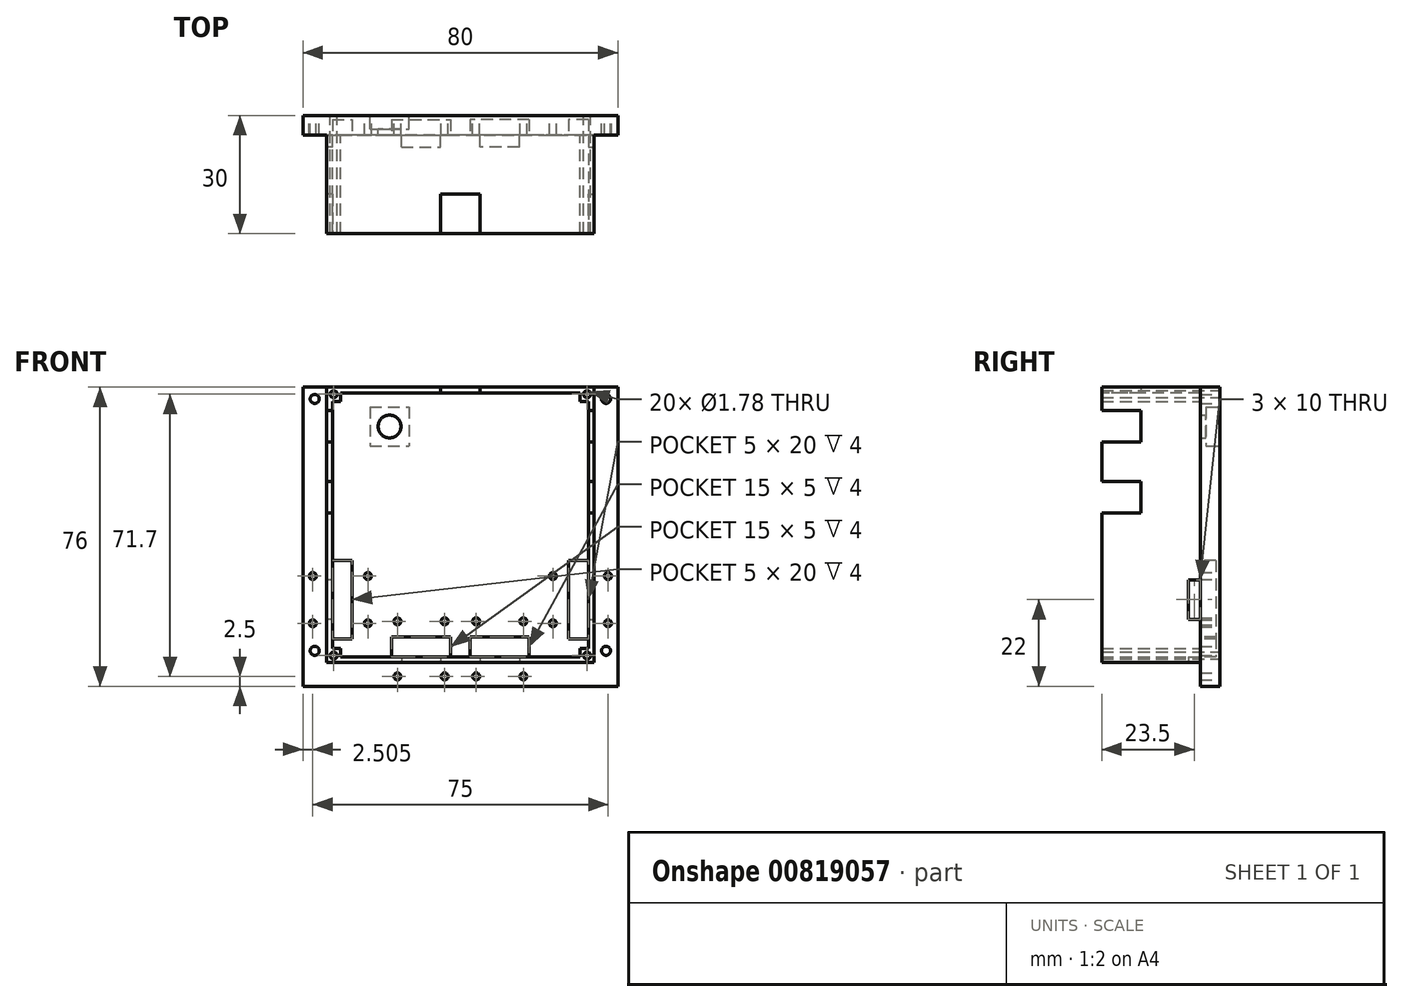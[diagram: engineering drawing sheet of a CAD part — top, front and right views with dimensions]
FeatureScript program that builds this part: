
annotation { "Feature Type Name" : "Feature", "Feature Type Description" : "" }
export const myFeature = defineFeature(function(context is Context, id is Id, definition is map)
    precondition{}
    {
        {
            var Q0;
            Q0=qCreatedBy(makeId("Front.planeOp"),FACE);
            var sketch = newSketch(context, id + "F0", { "sketchPlane" : qUnion([Q0])});
            skCircle(sketch, "E0", {"center": v(-20.58, 35.7) * mm, "radius": 0.89 * mm});
            skCircle(sketch, "E1", {"center": v(-25.88, -10.5) * mm, "radius": 0.89 * mm});
            skCircle(sketch, "E2", {"center": v(-11.88, -10.5) * mm, "radius": 0.89 * mm});
            skCircle(sketch, "E3", {"center": v(-11.88, -22.5) * mm, "radius": 0.89 * mm});
            skCircle(sketch, "E4", {"center": v(-25.88, -22.5) * mm, "radius": 0.89 * mm});
            skCircle(sketch, "E5", {"center": v(-25.38, -29.5) * mm, "radius": 1.14 * mm});
            skLineSegment(sketch, "E6", {"start": v(51.62, 37.5) * mm, "end": v(-28.38, 37.5) * mm});
            skLineSegment(sketch, "E7", {"start": v(-28.37, 37.5) * mm, "end": v(-28.38, -32.5) * mm});
            skLineSegment(sketch, "E8", {"start": v(51.63, -32.5) * mm, "end": v(-28.38, -32.5) * mm});
            skLineSegment(sketch, "E9.bottom", {"start": v(-28.38, -32.5) * mm, "end": v(-22.38, -32.5) * mm, "construction": true});
            skLineSegment(sketch, "E9.top", {"start": v(-28.38, -26.5) * mm, "end": v(-22.38, -26.5) * mm, "construction": true});
            skLineSegment(sketch, "E9.left", {"start": v(-28.38, -32.5) * mm, "end": v(-28.38, -26.5) * mm, "construction": true});
            skLineSegment(sketch, "E9.right", {"start": v(-22.38, -32.5) * mm, "end": v(-22.38, -26.5) * mm, "construction": true});
            skLineSegment(sketch, "E10", {"start": v(-28.37, -26.5) * mm, "end": v(-22.38, -32.5) * mm});
            skLineSegment(sketch, "E11", {"start": v(-28.38, -32.5) * mm, "end": v(-22.38, -26.5) * mm});
            skPoint(sketch, "E12", {"position": v(-28.38, 2.5) * mm});
            skLineSegment(sketch, "E13", {"start": v(11.62, 37.5) * mm, "end": v(-20.58, 37.5) * mm, "construction": true});
            skLineSegment(sketch, "E14", {"start": v(-20.58, 37.5) * mm, "end": v(-20.58, 35.7) * mm});
            skLineSegment(sketch, "E15", {"start": v(-11.88, -10.5) * mm, "end": v(-11.88, -22.5) * mm, "construction": true});
            skPoint(sketch, "E16", {"position": v(-11.88, -16.5) * mm});
            skLineSegment(sketch, "E17", {"start": v(-11.88, -16.5) * mm, "end": v(-28.38, -16.5) * mm, "construction": true});
            skLineSegment(sketch, "E18", {"start": v(-25.88, -22.5) * mm, "end": v(-25.88, -10.5) * mm, "construction": true});
            skPoint(sketch, "E19", {"position": v(-25.88, -16.5) * mm});
            skPoint(sketch, "E20", {"position": v(-20.88, -16.5) * mm});
            skLineSegment(sketch, "E21", {"start": v(-20.88, -16.5) * mm, "end": v(-20.88, -6.5) * mm, "construction": true});
            skLineSegment(sketch, "E22", {"start": v(-20.88, -6.5) * mm, "end": v(-15.88, -6.5) * mm, "construction": true});
            skLineSegment(sketch, "E23", {"start": v(-15.88, -6.5) * mm, "end": v(-15.88, -26.5) * mm, "construction": true});
            skLineSegment(sketch, "E24.bottom", {"start": v(-20.88, -6.5) * mm, "end": v(-15.88, -6.5) * mm});
            skLineSegment(sketch, "E24.top", {"start": v(-20.88, -26.5) * mm, "end": v(-15.88, -26.5) * mm});
            skLineSegment(sketch, "E24.left", {"start": v(-20.88, -6.5) * mm, "end": v(-20.88, -26.5) * mm});
            skLineSegment(sketch, "E24.right", {"start": v(-15.88, -6.5) * mm, "end": v(-15.88, -26.5) * mm});
            skLineSegment(sketch, "E25", {"start": v(-25.88, -10.5) * mm, "end": v(-28.38, -10.5) * mm, "construction": true});
            skLineSegment(sketch, "E26", {"start": v(-20.88, -6.5) * mm, "end": v(-28.38, -6.5) * mm, "construction": true});
            skLineSegment(sketch, "E27", {"start": v(51.62, 37.5) * mm, "end": v(51.63, -32.5) * mm});
            skLineSegment(sketch, "E28", {"start": v(11.62, 37.5) * mm, "end": v(11.62, 27.5) * mm, "construction": true});
            skLineSegment(sketch, "E29.bottom", {"start": v(-28.38, 37.5) * mm, "end": v(-22.38, 37.5) * mm, "construction": true});
            skLineSegment(sketch, "E29.top", {"start": v(-28.38, 31.5) * mm, "end": v(-22.38, 31.5) * mm, "construction": true});
            skLineSegment(sketch, "E29.left", {"start": v(-28.38, 37.5) * mm, "end": v(-28.38, 31.5) * mm, "construction": true});
            skLineSegment(sketch, "E29.right", {"start": v(-22.38, 37.5) * mm, "end": v(-22.38, 31.5) * mm, "construction": true});
            skLineSegment(sketch, "E30", {"start": v(-28.38, 37.5) * mm, "end": v(-22.38, 31.5) * mm, "construction": true});
            skLineSegment(sketch, "E31", {"start": v(-28.38, 31.5) * mm, "end": v(-22.38, 37.5) * mm, "construction": true});
            skCircle(sketch, "E32", {"center": v(-25.38, 34.5) * mm, "radius": 1.14 * mm});
            skCircle(sketch, "E33.MirrorC", {"center": v(48.62, -29.5) * mm, "radius": 1.14 * mm});
            skCircle(sketch, "E34.MirrorC", {"center": v(49.13, -22.5) * mm, "radius": 0.89 * mm});
            skLineSegment(sketch, "E35.MirrorCS", {"start": v(39.13, -6.5) * mm, "end": v(39.13, -26.5) * mm});
            skLineSegment(sketch, "E36.MirrorCS", {"start": v(44.13, -6.5) * mm, "end": v(39.13, -6.5) * mm});
            skLineSegment(sketch, "E37.MirrorCS", {"start": v(44.13, -6.5) * mm, "end": v(44.13, -26.5) * mm});
            skPoint(sketch, "E38.MirrorP", {"position": v(44.13, -16.5) * mm});
            skLineSegment(sketch, "E39.MirrorCS", {"start": v(44.13, -6.5) * mm, "end": v(39.13, -6.5) * mm, "construction": true});
            skLineSegment(sketch, "E40.MirrorCS", {"start": v(35.12, -10.5) * mm, "end": v(35.12, -22.5) * mm, "construction": true});
            skLineSegment(sketch, "E41.MirrorCS", {"start": v(44.13, -26.5) * mm, "end": v(39.13, -26.5) * mm});
            skLineSegment(sketch, "E42.MirrorCS", {"start": v(44.13, -16.5) * mm, "end": v(44.13, -6.5) * mm, "construction": true});
            skCircle(sketch, "E43.MirrorC", {"center": v(35.12, -22.5) * mm, "radius": 0.89 * mm});
            skCircle(sketch, "E44.MirrorC", {"center": v(35.12, -10.5) * mm, "radius": 0.89 * mm});
            skPoint(sketch, "E45.MirrorP", {"position": v(49.13, -16.5) * mm});
            skPoint(sketch, "E46.MirrorP", {"position": v(35.12, -16.5) * mm});
            skCircle(sketch, "E47.MirrorC", {"center": v(49.13, -10.5) * mm, "radius": 0.89 * mm});
            skLineSegment(sketch, "E48.MirrorCS", {"start": v(49.12, -22.5) * mm, "end": v(49.12, -10.5) * mm, "construction": true});
            skLineSegment(sketch, "E49.MirrorCS", {"start": v(39.13, -6.5) * mm, "end": v(39.13, -26.5) * mm, "construction": true});
            skPoint(sketch, "E50.MirrorP", {"position": v(51.63, 2.5) * mm});
            skCircle(sketch, "E51.MirrorC", {"center": v(48.63, 34.5) * mm, "radius": 1.14 * mm});
            skCircle(sketch, "E52.MirrorC", {"center": v(43.83, 35.7) * mm, "radius": 0.89 * mm});
            skLineSegment(sketch, "E53", {"start": v(44.13, -26.5) * mm, "end": v(45.63, -26.5) * mm, "construction": true});
            skLineSegment(sketch, "E54", {"start": v(45.63, -26.5) * mm, "end": v(45.63, -32.5) * mm});
            skLineSegment(sketch, "E55", {"start": v(45.63, -26.5) * mm, "end": v(45.63, 37.5) * mm});
            skLineSegment(sketch, "E56", {"start": v(-20.88, -26.5) * mm, "end": v(-22.38, -26.5) * mm, "construction": true});
            skLineSegment(sketch, "E57.bottom", {"start": v(-22.38, 37.5) * mm, "end": v(45.62, 37.5) * mm});
            skLineSegment(sketch, "E57.top", {"start": v(-22.38, -32.5) * mm, "end": v(45.63, -32.5) * mm});
            skLineSegment(sketch, "E57.left", {"start": v(-22.38, 37.5) * mm, "end": v(-22.38, -32.5) * mm});
            skLineSegment(sketch, "E57.right", {"start": v(45.63, 37.5) * mm, "end": v(45.63, -32.5) * mm});
            skLineSegment(sketch, "E58", {"start": v(-20.58, 35.7) * mm, "end": v(-18.78, 35.7) * mm, "construction": true});
            skLineSegment(sketch, "E59", {"start": v(-18.78, 35.7) * mm, "end": v(-18.78, 33.9) * mm, "construction": true});
            skLineSegment(sketch, "E60.bottom", {"start": v(-18.78, 33.9) * mm, "end": v(-22.38, 33.9) * mm});
            skLineSegment(sketch, "E60.top", {"start": v(-18.78, 37.5) * mm, "end": v(-22.38, 37.5) * mm});
            skLineSegment(sketch, "E60.left", {"start": v(-18.78, 33.9) * mm, "end": v(-18.78, 37.5) * mm});
            skLineSegment(sketch, "E60.right", {"start": v(-22.38, 33.9) * mm, "end": v(-22.38, 37.5) * mm});
            skLineSegment(sketch, "E61", {"start": v(43.83, 35.7) * mm, "end": v(42.02, 35.7) * mm, "construction": true});
            skLineSegment(sketch, "E62", {"start": v(42.03, 35.7) * mm, "end": v(42.03, 33.9) * mm, "construction": true});
            skLineSegment(sketch, "E63.bottom", {"start": v(42.02, 33.9) * mm, "end": v(45.62, 33.9) * mm});
            skLineSegment(sketch, "E63.top", {"start": v(42.02, 37.5) * mm, "end": v(45.62, 37.5) * mm});
            skLineSegment(sketch, "E63.left", {"start": v(42.03, 33.9) * mm, "end": v(42.03, 37.5) * mm});
            skLineSegment(sketch, "E63.right", {"start": v(45.63, 33.9) * mm, "end": v(45.63, 37.5) * mm});
            skLineSegment(sketch, "E64", {"start": v(11.63, -32.5) * mm, "end": v(13.43, -32.5) * mm});
            skLineSegment(sketch, "E65", {"start": v(44.13, -16.5) * mm, "end": v(47.13, -16.5) * mm, "construction": true});
            skLineSegment(sketch, "E66.bottom", {"start": v(43.13, -11.5) * mm, "end": v(47.13, -11.5) * mm});
            skLineSegment(sketch, "E66.top", {"start": v(43.13, -21.5) * mm, "end": v(47.13, -21.5) * mm});
            skLineSegment(sketch, "E66.left", {"start": v(43.13, -11.5) * mm, "end": v(43.13, -21.5) * mm});
            skLineSegment(sketch, "E66.right", {"start": v(47.13, -11.5) * mm, "end": v(47.13, -21.5) * mm});
            skPoint(sketch, "E67", {"position": v(47.13, -16.5) * mm});
            skLineSegment(sketch, "E68.MirrorCS", {"start": v(-19.88, -21.5) * mm, "end": v(-23.88, -21.5) * mm});
            skLineSegment(sketch, "E69.MirrorCS", {"start": v(-19.87, -11.5) * mm, "end": v(-19.87, -21.5) * mm});
            skLineSegment(sketch, "E70.MirrorCS", {"start": v(-23.87, -11.5) * mm, "end": v(-23.87, -21.5) * mm});
            skLineSegment(sketch, "E71.MirrorCS", {"start": v(-19.88, -11.5) * mm, "end": v(-23.88, -11.5) * mm});
            skLineSegment(sketch, "E72.bottom", {"start": v(41.62, 31.5) * mm, "end": v(45.62, 31.5) * mm});
            skLineSegment(sketch, "E72.top", {"start": v(41.62, 23.5) * mm, "end": v(45.62, 23.5) * mm});
            skLineSegment(sketch, "E72.left", {"start": v(41.63, 31.5) * mm, "end": v(41.63, 23.5) * mm});
            skLineSegment(sketch, "E72.right", {"start": v(45.63, 31.5) * mm, "end": v(45.63, 23.5) * mm});
            skPoint(sketch, "E73", {"position": v(45.62, 27.5) * mm});
            skLineSegment(sketch, "E74.MirrorCS", {"start": v(-18.37, 23.5) * mm, "end": v(-22.37, 23.5) * mm});
            skLineSegment(sketch, "E75.MirrorCS", {"start": v(-22.38, 31.5) * mm, "end": v(-22.38, 23.5) * mm});
            skLineSegment(sketch, "E76.MirrorCS", {"start": v(-18.37, 31.5) * mm, "end": v(-22.38, 31.5) * mm});
            skLineSegment(sketch, "E77.MirrorCS", {"start": v(-18.38, 31.5) * mm, "end": v(-18.38, 23.5) * mm});
            skLineSegment(sketch, "E78.bottom", {"start": v(6.62, 37.5) * mm, "end": v(16.62, 37.5) * mm});
            skLineSegment(sketch, "E78.top", {"start": v(6.62, 33.5) * mm, "end": v(16.62, 33.5) * mm});
            skLineSegment(sketch, "E78.left", {"start": v(6.62, 37.5) * mm, "end": v(6.62, 33.5) * mm});
            skLineSegment(sketch, "E78.right", {"start": v(16.62, 37.5) * mm, "end": v(16.62, 33.5) * mm});
            skPoint(sketch, "E79", {"position": v(11.62, 37.5) * mm});
            skLineSegment(sketch, "E80", {"start": v(-22.38, 37.5) * mm, "end": v(-20.58, 37.5) * mm});
            skLineSegment(sketch, "E81", {"start": v(11.62, 27.5) * mm, "end": v(45.62, 27.5) * mm, "construction": true});
            skLineSegment(sketch, "E82", {"start": v(-5.88, -32.5) * mm, "end": v(-5.88, -31) * mm, "construction": true});
            skLineSegment(sketch, "E83.bottom", {"start": v(-5.88, -26) * mm, "end": v(9.12, -26) * mm});
            skLineSegment(sketch, "E83.top", {"start": v(-5.88, -31) * mm, "end": v(9.12, -31) * mm});
            skLineSegment(sketch, "E83.left", {"start": v(-5.88, -26) * mm, "end": v(-5.88, -31) * mm});
            skLineSegment(sketch, "E83.right", {"start": v(9.12, -26) * mm, "end": v(9.12, -31) * mm});
            skPoint(sketch, "E84", {"position": v(1.62, -26) * mm});
            skLineSegment(sketch, "E85", {"start": v(1.62, -26) * mm, "end": v(1.62, -22) * mm, "construction": true});
            skLineSegment(sketch, "E86", {"start": v(-4.38, -22) * mm, "end": v(7.63, -22) * mm, "construction": true});
            skPoint(sketch, "E87", {"position": v(1.62, -22) * mm});
            skCircle(sketch, "E88", {"center": v(-4.38, -22) * mm, "radius": 0.89 * mm});
            skCircle(sketch, "E89", {"center": v(7.63, -22) * mm, "radius": 0.89 * mm});
            skLineSegment(sketch, "E90.bottom", {"start": v(-28.37, -32.5) * mm, "end": v(51.63, -32.5) * mm});
            skLineSegment(sketch, "E90.top", {"start": v(-28.37, -38.5) * mm, "end": v(51.63, -38.5) * mm});
            skLineSegment(sketch, "E90.left", {"start": v(-28.38, -32.5) * mm, "end": v(-28.38, -38.5) * mm});
            skLineSegment(sketch, "E90.right", {"start": v(51.63, -32.5) * mm, "end": v(51.63, -38.5) * mm});
            skLineSegment(sketch, "E91.bottom", {"start": v(-3.37, -31) * mm, "end": v(6.63, -31) * mm});
            skLineSegment(sketch, "E91.top", {"start": v(-3.38, -34) * mm, "end": v(6.63, -34) * mm});
            skLineSegment(sketch, "E91.left", {"start": v(-3.38, -31) * mm, "end": v(-3.38, -34) * mm});
            skLineSegment(sketch, "E91.right", {"start": v(6.63, -31) * mm, "end": v(6.63, -34) * mm});
            skPoint(sketch, "E92", {"position": v(1.63, -31) * mm});
            skPoint(sketch, "E93", {"position": v(1.62, -31) * mm});
            skLineSegment(sketch, "E94", {"start": v(1.63, -31) * mm, "end": v(1.63, -38.5) * mm, "construction": true});
            skLineSegment(sketch, "E95", {"start": v(1.63, -38.5) * mm, "end": v(1.63, -36) * mm, "construction": true});
            skLineSegment(sketch, "E96", {"start": v(-4.38, -36) * mm, "end": v(7.63, -36) * mm, "construction": true});
            skPoint(sketch, "E97", {"position": v(1.62, -36) * mm});
            skCircle(sketch, "E98", {"center": v(-4.38, -36) * mm, "radius": 0.89 * mm});
            skCircle(sketch, "E99", {"center": v(7.63, -36) * mm, "radius": 0.89 * mm});
            skCircle(sketch, "E100.MirrorC", {"center": v(15.62, -36) * mm, "radius": 0.89 * mm});
            skCircle(sketch, "E101.MirrorC", {"center": v(27.63, -36) * mm, "radius": 0.89 * mm});
            skLineSegment(sketch, "E102.MirrorCS", {"start": v(21.62, -38.5) * mm, "end": v(21.62, -36) * mm, "construction": true});
            skLineSegment(sketch, "E103.MirrorCS", {"start": v(26.62, -31) * mm, "end": v(26.62, -34) * mm});
            skLineSegment(sketch, "E104.MirrorCS", {"start": v(29.12, -32.5) * mm, "end": v(29.12, -31) * mm, "construction": true});
            skLineSegment(sketch, "E105.MirrorCS", {"start": v(29.12, -31) * mm, "end": v(14.12, -31) * mm});
            skPoint(sketch, "E106.MirrorP", {"position": v(21.62, -31) * mm});
            skLineSegment(sketch, "E107.MirrorCS", {"start": v(11.62, -32.5) * mm, "end": v(9.82, -32.5) * mm});
            skCircle(sketch, "E108.MirrorC", {"center": v(27.63, -22) * mm, "radius": 0.89 * mm});
            skCircle(sketch, "E109.MirrorC", {"center": v(15.62, -22) * mm, "radius": 0.89 * mm});
            skPoint(sketch, "E110.MirrorP", {"position": v(21.62, -36) * mm});
            skPoint(sketch, "E111.MirrorP", {"position": v(21.63, -31) * mm});
            skPoint(sketch, "E112.MirrorP", {"position": v(21.63, -26) * mm});
            skLineSegment(sketch, "E113.MirrorCS", {"start": v(21.63, -26) * mm, "end": v(21.63, -22) * mm, "construction": true});
            skLineSegment(sketch, "E114.MirrorCS", {"start": v(29.12, -26) * mm, "end": v(29.12, -31) * mm});
            skLineSegment(sketch, "E115.MirrorCS", {"start": v(27.63, -36) * mm, "end": v(15.62, -36) * mm, "construction": true});
            skLineSegment(sketch, "E116.MirrorCS", {"start": v(26.62, -34) * mm, "end": v(16.62, -34) * mm});
            skLineSegment(sketch, "E117.MirrorCS", {"start": v(21.62, -31) * mm, "end": v(21.62, -38.5) * mm, "construction": true});
            skLineSegment(sketch, "E118.MirrorCS", {"start": v(27.63, -22) * mm, "end": v(15.62, -22) * mm, "construction": true});
            skLineSegment(sketch, "E119.MirrorCS", {"start": v(29.12, -26) * mm, "end": v(14.12, -26) * mm});
            skLineSegment(sketch, "E120.MirrorCS", {"start": v(16.62, -31) * mm, "end": v(16.62, -34) * mm});
            skPoint(sketch, "E121.MirrorP", {"position": v(21.63, -22) * mm});
            skLineSegment(sketch, "E122.MirrorCS", {"start": v(26.62, -31) * mm, "end": v(16.62, -31) * mm});
            skLineSegment(sketch, "E123.MirrorCS", {"start": v(14.12, -26) * mm, "end": v(14.12, -31) * mm});
            skLineSegment(sketch, "E124", {"start": v(-28.38, 2.5) * mm, "end": v(51.63, 2.5) * mm, "construction": true});
            skCircle(sketch, "E125.MirrorC", {"center": v(43.82, -30.7) * mm, "radius": 0.89 * mm});
            skLineSegment(sketch, "E126.MirrorCS", {"start": v(42.02, -28.9) * mm, "end": v(45.63, -28.9) * mm});
            skLineSegment(sketch, "E127.MirrorCS", {"start": v(45.63, -28.9) * mm, "end": v(45.63, -32.5) * mm});
            skLineSegment(sketch, "E128.MirrorCS", {"start": v(42.03, -28.9) * mm, "end": v(42.03, -32.5) * mm});
            skLineSegment(sketch, "E129.MirrorCS", {"start": v(42.02, -32.5) * mm, "end": v(45.62, -32.5) * mm});
            skLineSegment(sketch, "E130.MirrorCS", {"start": v(42.03, -30.7) * mm, "end": v(42.03, -28.9) * mm, "construction": true});
            skLineSegment(sketch, "E131.MirrorCS", {"start": v(43.82, -30.7) * mm, "end": v(42.02, -30.7) * mm, "construction": true});
            skLineSegment(sketch, "E132.MirrorCS", {"start": v(-18.78, -28.9) * mm, "end": v(-18.78, -32.5) * mm});
            skLineSegment(sketch, "E133.MirrorCS", {"start": v(-20.58, -30.7) * mm, "end": v(-18.77, -30.7) * mm, "construction": true});
            skLineSegment(sketch, "E134.MirrorCS", {"start": v(-18.78, -30.7) * mm, "end": v(-18.78, -28.9) * mm, "construction": true});
            skLineSegment(sketch, "E135.MirrorCS", {"start": v(-18.77, -28.9) * mm, "end": v(-22.38, -28.9) * mm});
            skCircle(sketch, "E136.MirrorC", {"center": v(-20.58, -30.7) * mm, "radius": 0.89 * mm});
            skLineSegment(sketch, "E137.MirrorCS", {"start": v(-18.78, -32.5) * mm, "end": v(-22.38, -32.5) * mm});
            skLineSegment(sketch, "E138.MirrorCS", {"start": v(-22.38, -32.5) * mm, "end": v(-20.58, -32.5) * mm});
            skLineSegment(sketch, "E139.MirrorCS", {"start": v(-20.58, -32.5) * mm, "end": v(-20.58, -30.7) * mm});
            skLineSegment(sketch, "E140.MirrorCS", {"start": v(-22.38, -28.9) * mm, "end": v(-22.38, -32.5) * mm});
            skLineSegment(sketch, "E141", {"start": v(27.62, 27.5) * mm, "end": v(27.62, 9.5) * mm, "construction": true});
            skLineSegment(sketch, "E142", {"start": v(27.62, 9.5) * mm, "end": v(45.62, 9.5) * mm, "construction": true});
            skLineSegment(sketch, "E143.bottom", {"start": v(41.62, 13.5) * mm, "end": v(45.62, 13.5) * mm});
            skLineSegment(sketch, "E143.top", {"start": v(41.62, 5.5) * mm, "end": v(45.62, 5.5) * mm});
            skLineSegment(sketch, "E143.left", {"start": v(41.62, 13.5) * mm, "end": v(41.62, 5.5) * mm});
            skLineSegment(sketch, "E143.right", {"start": v(45.62, 13.5) * mm, "end": v(45.62, 5.5) * mm});
            skPoint(sketch, "E144", {"position": v(45.62, 9.5) * mm});
            skPoint(sketch, "E145.MirrorP", {"position": v(-22.38, 9.5) * mm});
            skLineSegment(sketch, "E146.MirrorCS", {"start": v(-22.37, 13.5) * mm, "end": v(-22.38, 5.5) * mm});
            skLineSegment(sketch, "E147.MirrorCS", {"start": v(-18.38, 13.5) * mm, "end": v(-18.38, 5.5) * mm});
            skLineSegment(sketch, "E148.MirrorCS", {"start": v(-18.38, 13.5) * mm, "end": v(-22.38, 13.5) * mm});
            skLineSegment(sketch, "E149.MirrorCS", {"start": v(-18.38, 5.5) * mm, "end": v(-22.38, 5.5) * mm});
            skLineSegment(sketch, "E150", {"start": v(11.62, 27.5) * mm, "end": v(-6.38, 27.5) * mm, "construction": true});
            skCircle(sketch, "E151", {"center": v(-6.38, 27.5) * mm, "radius": 2.9 * mm, "construction": true});
            skLineSegment(sketch, "E152", {"start": v(-6.38, 27.5) * mm, "end": v(-6.38, 32.5) * mm, "construction": true});
            skLineSegment(sketch, "E153", {"start": v(-6.38, 32.5) * mm, "end": v(-11.38, 32.5) * mm, "construction": true});
            skLineSegment(sketch, "E154.bottom", {"start": v(-11.38, 32.5) * mm, "end": v(-1.38, 32.5) * mm});
            skLineSegment(sketch, "E154.top", {"start": v(-11.38, 22.5) * mm, "end": v(-1.38, 22.5) * mm});
            skLineSegment(sketch, "E154.left", {"start": v(-11.38, 32.5) * mm, "end": v(-11.38, 22.5) * mm});
            skLineSegment(sketch, "E154.right", {"start": v(-1.38, 32.5) * mm, "end": v(-1.38, 22.5) * mm});
            skSolve(sketch);
        }
        {
            var Q0;
            Q0=qCreatedBy(makeId("Front.planeOp"),FACE);
            var sketch = newSketch(context, id + "F1", { "sketchPlane" : qUnion([Q0])});
            skLineSegment(sketch, "E155.0", {"start": v(51.62, 37.5) * mm, "end": v(-28.38, 37.5) * mm});
            skLineSegment(sketch, "E155.1", {"start": v(-28.37, 37.5) * mm, "end": v(-28.38, -32.5) * mm});
            skLineSegment(sketch, "E155.2", {"start": v(51.62, 37.5) * mm, "end": v(51.63, -32.5) * mm});
            skLineSegment(sketch, "E156.0", {"start": v(-28.38, -32.5) * mm, "end": v(-28.38, -38.5) * mm});
            skLineSegment(sketch, "E156.1", {"start": v(-28.37, -38.5) * mm, "end": v(51.63, -38.5) * mm});
            skLineSegment(sketch, "E156.2", {"start": v(51.63, -32.5) * mm, "end": v(51.63, -38.5) * mm});
            skSolve(sketch);
        }
        {
            var Q0;
            Q0=qCreatedBy(makeId("Front.planeOp"),FACE);
            var sketch = newSketch(context, id + "F2", { "sketchPlane" : qUnion([Q0])});
            skLineSegment(sketch, "E157.4", {"start": v(-20.88, -6.5) * mm, "end": v(-15.88, -6.5) * mm});
            skLineSegment(sketch, "E157.5", {"start": v(-20.88, -6.5) * mm, "end": v(-20.88, -26.5) * mm});
            skLineSegment(sketch, "E157.6", {"start": v(-15.88, -6.5) * mm, "end": v(-15.88, -26.5) * mm});
            skLineSegment(sketch, "E157.7", {"start": v(-20.88, -26.5) * mm, "end": v(-15.88, -26.5) * mm});
            skLineSegment(sketch, "E158.5", {"start": v(44.13, -6.5) * mm, "end": v(44.13, -26.5) * mm});
            skLineSegment(sketch, "E158.6", {"start": v(44.13, -6.5) * mm, "end": v(39.13, -6.5) * mm});
            skLineSegment(sketch, "E158.7", {"start": v(39.13, -6.5) * mm, "end": v(39.13, -26.5) * mm});
            skLineSegment(sketch, "E158.8", {"start": v(44.13, -26.5) * mm, "end": v(39.13, -26.5) * mm});
            skLineSegment(sketch, "E159.0", {"start": v(-5.88, -26) * mm, "end": v(9.12, -26) * mm});
            skLineSegment(sketch, "E159.1", {"start": v(-5.88, -26) * mm, "end": v(-5.88, -31) * mm});
            skLineSegment(sketch, "E159.2", {"start": v(-5.88, -31) * mm, "end": v(9.12, -31) * mm});
            skLineSegment(sketch, "E159.3", {"start": v(9.12, -26) * mm, "end": v(9.12, -31) * mm});
            skLineSegment(sketch, "E160.0", {"start": v(29.12, -26) * mm, "end": v(14.12, -26) * mm});
            skLineSegment(sketch, "E160.1", {"start": v(14.12, -26) * mm, "end": v(14.12, -31) * mm});
            skLineSegment(sketch, "E160.2", {"start": v(29.12, -31) * mm, "end": v(14.12, -31) * mm});
            skLineSegment(sketch, "E160.3", {"start": v(29.12, -26) * mm, "end": v(29.12, -31) * mm});
            skSolve(sketch);
        }
        {
            var Q0;
            Q0=qCreatedBy(makeId("Front.planeOp"),FACE);
            var sketch = newSketch(context, id + "F3", { "sketchPlane" : qUnion([Q0])});
            skCircle(sketch, "E161.10", {"center": v(-11.88, -10.5) * mm, "radius": 0.89 * mm});
            skCircle(sketch, "E161.11", {"center": v(-25.88, -10.5) * mm, "radius": 0.89 * mm});
            skCircle(sketch, "E161.12", {"center": v(-25.88, -22.5) * mm, "radius": 0.89 * mm});
            skCircle(sketch, "E161.13", {"center": v(-11.88, -22.5) * mm, "radius": 0.89 * mm});
            skCircle(sketch, "E161.22", {"center": v(-25.38, -29.5) * mm, "radius": 1.14 * mm});
            skCircle(sketch, "E162.0", {"center": v(-25.38, 34.5) * mm, "radius": 1.14 * mm});
            skCircle(sketch, "E162.4", {"center": v(48.63, 34.5) * mm, "radius": 1.14 * mm});
            skCircle(sketch, "E162.5", {"center": v(35.12, -10.5) * mm, "radius": 0.89 * mm});
            skCircle(sketch, "E162.6", {"center": v(35.12, -22.5) * mm, "radius": 0.89 * mm});
            skCircle(sketch, "E162.7", {"center": v(49.13, -10.5) * mm, "radius": 0.89 * mm});
            skCircle(sketch, "E162.8", {"center": v(49.13, -22.5) * mm, "radius": 0.89 * mm});
            skCircle(sketch, "E162.9", {"center": v(48.62, -29.5) * mm, "radius": 1.14 * mm});
            skCircle(sketch, "E163.0", {"center": v(-20.58, 35.7) * mm, "radius": 0.89 * mm});
            skCircle(sketch, "E163.1", {"center": v(43.83, 35.7) * mm, "radius": 0.89 * mm});
            skCircle(sketch, "E164.0", {"center": v(-20.58, -30.7) * mm, "radius": 0.89 * mm});
            skCircle(sketch, "E164.1", {"center": v(-4.38, -22) * mm, "radius": 0.89 * mm});
            skCircle(sketch, "E164.2", {"center": v(7.63, -22) * mm, "radius": 0.89 * mm});
            skCircle(sketch, "E164.3", {"center": v(-4.38, -36) * mm, "radius": 0.89 * mm});
            skCircle(sketch, "E164.4", {"center": v(7.63, -36) * mm, "radius": 0.89 * mm});
            skCircle(sketch, "E164.5", {"center": v(15.62, -22) * mm, "radius": 0.89 * mm});
            skCircle(sketch, "E164.6", {"center": v(27.63, -22) * mm, "radius": 0.89 * mm});
            skCircle(sketch, "E164.7", {"center": v(27.63, -36) * mm, "radius": 0.89 * mm});
            skCircle(sketch, "E164.8", {"center": v(15.62, -36) * mm, "radius": 0.89 * mm});
            skCircle(sketch, "E165.0", {"center": v(43.82, -30.7) * mm, "radius": 0.89 * mm});
            skCircle(sketch, "E166.0", {"center": v(-6.38, 27.5) * mm, "radius": 2.9 * mm});
            skSolve(sketch);
        }
        {
            var Q0;
            Q0=qSketchRegion(id+"F1",true);
            extrude(context, id + "F4", {"entities" : qUnion([Q0]), "depth" : 5 * mm, "offsetDistance" : 25 * mm});
        }
        {
            var Q0;
            Q0=qCreatedBy(makeId("Front.planeOp"),FACE);
            var sketch = newSketch(context, id + "F5", { "sketchPlane" : qUnion([Q0])});
            skLineSegment(sketch, "E167.0", {"start": v(-22.38, 37.5) * mm, "end": v(-22.38, -32.5) * mm});
            skLineSegment(sketch, "E167.1", {"start": v(-22.38, 37.5) * mm, "end": v(45.62, 37.5) * mm});
            skLineSegment(sketch, "E167.2", {"start": v(45.63, -26.5) * mm, "end": v(45.63, 37.5) * mm});
            skLineSegment(sketch, "E167.4", {"start": v(45.63, 37.5) * mm, "end": v(45.63, -32.5) * mm});
            skLineSegment(sketch, "E168.0", {"start": v(-22.38, -32.5) * mm, "end": v(45.63, -32.5) * mm});
            skLineSegment(sketch, "E169.0", {"start": v(-20.88, 36) * mm, "end": v(44.13, 36) * mm});
            skLineSegment(sketch, "E169.1", {"start": v(-20.88, 36) * mm, "end": v(-20.88, -31) * mm});
            skLineSegment(sketch, "E169.2", {"start": v(-20.88, -31) * mm, "end": v(44.13, -31) * mm});
            skLineSegment(sketch, "E169.3", {"start": v(44.13, 36) * mm, "end": v(44.13, -31) * mm});
            skSolve(sketch);
        }
        {
            var Q0;
            Q0=qCreatedBy(makeId("Front.planeOp"),FACE);
            var sketch = newSketch(context, id + "F6", { "sketchPlane" : qUnion([Q0])});
            skLineSegment(sketch, "E170.0", {"start": v(-18.78, 33.9) * mm, "end": v(-18.78, 37.5) * mm});
            skLineSegment(sketch, "E170.1", {"start": v(-18.78, 33.9) * mm, "end": v(-22.38, 33.9) * mm});
            skLineSegment(sketch, "E170.2", {"start": v(-18.78, 37.5) * mm, "end": v(-22.38, 37.5) * mm});
            skLineSegment(sketch, "E170.3", {"start": v(-22.38, 33.9) * mm, "end": v(-22.38, 37.5) * mm});
            skLineSegment(sketch, "E171.0", {"start": v(42.02, 33.9) * mm, "end": v(45.62, 33.9) * mm});
            skLineSegment(sketch, "E171.1", {"start": v(42.03, 33.9) * mm, "end": v(42.03, 37.5) * mm});
            skLineSegment(sketch, "E171.2", {"start": v(45.63, 33.9) * mm, "end": v(45.63, 37.5) * mm});
            skLineSegment(sketch, "E171.3", {"start": v(42.02, 37.5) * mm, "end": v(45.62, 37.5) * mm});
            skLineSegment(sketch, "E172.0", {"start": v(-18.77, -28.9) * mm, "end": v(-22.38, -28.9) * mm});
            skLineSegment(sketch, "E172.1", {"start": v(-18.78, -28.9) * mm, "end": v(-18.78, -32.5) * mm});
            skLineSegment(sketch, "E172.2", {"start": v(-18.78, -32.5) * mm, "end": v(-22.38, -32.5) * mm});
            skLineSegment(sketch, "E172.3", {"start": v(-22.38, -28.9) * mm, "end": v(-22.38, -32.5) * mm});
            skPoint(sketch, "E172.4", {"position": v(-20.57, -28.9) * mm});
            skLineSegment(sketch, "E173.0", {"start": v(42.02, -28.9) * mm, "end": v(45.63, -28.9) * mm});
            skLineSegment(sketch, "E173.1", {"start": v(42.03, -28.9) * mm, "end": v(42.03, -32.5) * mm});
            skLineSegment(sketch, "E173.2", {"start": v(45.63, -28.9) * mm, "end": v(45.63, -32.5) * mm});
            skLineSegment(sketch, "E173.3", {"start": v(42.02, -32.5) * mm, "end": v(45.62, -32.5) * mm});
            skSolve(sketch);
        }
        {
            var Q0;
            Q0 = qSketchRegion(id + "F5", true);
            extrude(context, id + "F7", {"entities" : qUnion([Q0]), "operationType" : NewBodyOperationType.ADD, "depth" : 30 * mm, "offsetDistance" : 25 * mm});
        }
        {
            var Q0;
            {var subQ0=sQuery(id+"F1.wireOp",EDGE,"E156.2");var subQ1=sQuery(id+"F1.wireOp",EDGE,"E155.2");var subQ2=sQuery(id+"F1.wireOp",EDGE,"E156.0");var subQ3=sQuery(id+"F1.wireOp",EDGE,"E155.1");var subQ4=sQuery(id+"F1.wireOp",EDGE,"E156.1");var subQ5=sQuery(id+"F1.wireOp",EDGE,"E155.0");Q0=makeQuery(id+"F7.boolean.opBoolean","SPLIT",FACE,{"disambiguationData":[TD([makeQuery(id+"F4.opExtrude","SWEPT_FACE",FACE,{"disambiguationData":[OSD([subQ5])]})])],"derivedFrom":makeQuery(id+"F4.opExtrude","CAP_FACE",FACE,{"disambiguationData":[OSD([subQ5,subQ3,subQ1,subQ2,subQ4,subQ0])],"isStart":false})});}
            var sketch = newSketch(context, id + "F8", { "sketchPlane" : qUnion([Q0])});
            skLineSegment(sketch, "E174.0", {"start": v(-20.88, -6.5) * mm, "end": v(-15.88, -6.5) * mm});
            skLineSegment(sketch, "E174.1", {"start": v(-15.88, -6.5) * mm, "end": v(-15.88, -26.5) * mm});
            skLineSegment(sketch, "E174.2", {"start": v(-20.88, -6.5) * mm, "end": v(-20.88, -26.5) * mm});
            skLineSegment(sketch, "E174.3", {"start": v(-20.88, -26.5) * mm, "end": v(-15.88, -26.5) * mm});
            skLineSegment(sketch, "E174.4", {"start": v(-5.88, -26) * mm, "end": v(9.12, -26) * mm});
            skLineSegment(sketch, "E174.5", {"start": v(-5.88, -26) * mm, "end": v(-5.88, -31) * mm});
            skLineSegment(sketch, "E174.6", {"start": v(-5.88, -31) * mm, "end": v(9.12, -31) * mm});
            skLineSegment(sketch, "E174.7", {"start": v(9.12, -26) * mm, "end": v(9.12, -31) * mm});
            skLineSegment(sketch, "E174.8", {"start": v(29.12, -26) * mm, "end": v(14.12, -26) * mm});
            skLineSegment(sketch, "E174.9", {"start": v(14.12, -26) * mm, "end": v(14.12, -31) * mm});
            skLineSegment(sketch, "E174.10", {"start": v(29.12, -31) * mm, "end": v(14.12, -31) * mm});
            skLineSegment(sketch, "E174.11", {"start": v(29.12, -26) * mm, "end": v(29.12, -31) * mm});
            skLineSegment(sketch, "E174.12", {"start": v(39.13, -6.5) * mm, "end": v(39.13, -26.5) * mm});
            skLineSegment(sketch, "E174.13", {"start": v(44.13, -6.5) * mm, "end": v(39.13, -6.5) * mm});
            skLineSegment(sketch, "E174.14", {"start": v(44.13, -26.5) * mm, "end": v(39.13, -26.5) * mm});
            skLineSegment(sketch, "E174.15", {"start": v(44.13, -6.5) * mm, "end": v(44.13, -26.5) * mm});
            skPoint(sketch, "E174.16", {"position": v(41.63, -6.5) * mm});
            skSolve(sketch);
        }
        {
            var Q0;
            Q0 = qSketchRegion(id + "F8", true);
            extrude(context, id + "F9", {"entities" : qUnion([Q0]), "operationType" : NewBodyOperationType.REMOVE, "oppositeDirection" : true, "depth" : 4 * mm, "offsetDistance" : 25 * mm});
        }
        {
            var Q0;
            Q0 = qSketchRegion(id + "F6", true);
            extrude(context, id + "F10", {"entities" : qUnion([Q0]), "operationType" : NewBodyOperationType.ADD, "depth" : 30 * mm, "offsetDistance" : 25 * mm});
        }
        {
            var Q0;
            {var subQ0=sQuery(id+"F1.wireOp",EDGE,"E156.2");var subQ1=sQuery(id+"F1.wireOp",EDGE,"E155.2");var subQ2=sQuery(id+"F1.wireOp",EDGE,"E156.0");var subQ3=sQuery(id+"F1.wireOp",EDGE,"E155.1");var subQ4=sQuery(id+"F1.wireOp",EDGE,"E156.1");var subQ5=sQuery(id+"F1.wireOp",EDGE,"E155.0");Q0=makeQuery(id+"F7.boolean.opBoolean","SPLIT",FACE,{"disambiguationData":[TD([makeQuery(id+"F4.opExtrude","SWEPT_FACE",FACE,{"disambiguationData":[OSD([subQ5])]})])],"derivedFrom":makeQuery(id+"F4.opExtrude","CAP_FACE",FACE,{"disambiguationData":[OSD([subQ5,subQ3,subQ1,subQ2,subQ4,subQ0])],"isStart":false})});}
            var sketch = newSketch(context, id + "F11", { "sketchPlane" : qUnion([Q0])});
            skLineSegment(sketch, "E175.0", {"start": v(-19.88, -11.5) * mm, "end": v(-23.88, -11.5) * mm});
            skLineSegment(sketch, "E175.1", {"start": v(-23.87, -11.5) * mm, "end": v(-23.87, -21.5) * mm});
            skLineSegment(sketch, "E175.2", {"start": v(-19.87, -11.5) * mm, "end": v(-19.87, -21.5) * mm});
            skLineSegment(sketch, "E175.3", {"start": v(-19.88, -21.5) * mm, "end": v(-23.88, -21.5) * mm});
            skLineSegment(sketch, "E175.4", {"start": v(43.13, -11.5) * mm, "end": v(47.13, -11.5) * mm});
            skLineSegment(sketch, "E175.5", {"start": v(43.13, -11.5) * mm, "end": v(43.13, -21.5) * mm});
            skLineSegment(sketch, "E175.6", {"start": v(47.13, -11.5) * mm, "end": v(47.13, -21.5) * mm});
            skLineSegment(sketch, "E175.7", {"start": v(43.13, -21.5) * mm, "end": v(47.13, -21.5) * mm});
            skLineSegment(sketch, "E176.0", {"start": v(26.62, -34) * mm, "end": v(16.62, -34) * mm});
            skLineSegment(sketch, "E176.1", {"start": v(16.62, -31) * mm, "end": v(16.62, -34) * mm});
            skLineSegment(sketch, "E176.2", {"start": v(26.62, -31) * mm, "end": v(26.62, -34) * mm});
            skLineSegment(sketch, "E177.0", {"start": v(26.62, -31) * mm, "end": v(16.62, -31) * mm});
            skLineSegment(sketch, "E178.0", {"start": v(6.63, -31) * mm, "end": v(6.63, -34) * mm});
            skLineSegment(sketch, "E178.1", {"start": v(-3.38, -31) * mm, "end": v(-3.38, -34) * mm});
            skLineSegment(sketch, "E178.2", {"start": v(-3.38, -34) * mm, "end": v(6.63, -34) * mm});
            skLineSegment(sketch, "E178.3", {"start": v(-3.37, -31) * mm, "end": v(6.63, -31) * mm});
            skSolve(sketch);
        }
        {
            var Q0;
            Q0 = qSketchRegion(id + "F11", true);
            extrude(context, id + "F12", {"entities" : qUnion([Q0]), "operationType" : NewBodyOperationType.REMOVE, "depth" : 3 * mm, "offsetDistance" : 25 * mm});
        }
        {
            var Q0;
            Q0=makeQuery(id+"F10.boolean.opBoolean","MERGE",FACE,{"derivedFrom":[makeQuery(id+"F7.opExtrude","CAP_FACE",FACE,{"disambiguationData":[OSD([sQuery(id+"F5.wireOp",EDGE,"E167.0"),sQuery(id+"F5.wireOp",EDGE,"E167.1"),sQuery(id+"F5.wireOp",EDGE,"E167.4"),sQuery(id+"F5.wireOp",EDGE,"E168.0"),sQuery(id+"F5.wireOp",EDGE,"E169.0"),sQuery(id+"F5.wireOp",EDGE,"E169.1"),sQuery(id+"F5.wireOp",EDGE,"E169.2"),sQuery(id+"F5.wireOp",EDGE,"E169.3")])],"isStart":false}),makeQuery(id+"F10.opExtrude","CAP_FACE",FACE,{"disambiguationData":[OSD([sQuery(id+"F6.wireOp",EDGE,"E170.0"),sQuery(id+"F6.wireOp",EDGE,"E170.1"),sQuery(id+"F6.wireOp",EDGE,"E170.2"),sQuery(id+"F6.wireOp",EDGE,"E170.3")])],"isStart":false}),makeQuery(id+"F10.opExtrude","CAP_FACE",FACE,{"disambiguationData":[OSD([sQuery(id+"F6.wireOp",EDGE,"E171.0"),sQuery(id+"F6.wireOp",EDGE,"E171.1"),sQuery(id+"F6.wireOp",EDGE,"E171.2"),sQuery(id+"F6.wireOp",EDGE,"E171.3")])],"isStart":false}),makeQuery(id+"F10.opExtrude","CAP_FACE",FACE,{"disambiguationData":[OSD([sQuery(id+"F6.wireOp",EDGE,"E172.0"),sQuery(id+"F6.wireOp",EDGE,"E172.1"),sQuery(id+"F6.wireOp",EDGE,"E172.2"),sQuery(id+"F6.wireOp",EDGE,"E172.3")])],"isStart":false}),makeQuery(id+"F10.opExtrude","CAP_FACE",FACE,{"disambiguationData":[OSD([sQuery(id+"F6.wireOp",EDGE,"E173.0"),sQuery(id+"F6.wireOp",EDGE,"E173.1"),sQuery(id+"F6.wireOp",EDGE,"E173.2"),sQuery(id+"F6.wireOp",EDGE,"E173.3")])],"isStart":false})]});
            var sketch = newSketch(context, id + "F13", { "sketchPlane" : qUnion([Q0])});
            skLineSegment(sketch, "E179.0", {"start": v(6.62, 33.5) * mm, "end": v(16.62, 33.5) * mm});
            skLineSegment(sketch, "E179.1", {"start": v(6.62, 37.5) * mm, "end": v(6.62, 33.5) * mm});
            skLineSegment(sketch, "E179.2", {"start": v(16.62, 37.5) * mm, "end": v(16.62, 33.5) * mm});
            skLineSegment(sketch, "E179.3", {"start": v(6.62, 37.5) * mm, "end": v(16.62, 37.5) * mm});
            skLineSegment(sketch, "E180.0", {"start": v(-18.38, 31.5) * mm, "end": v(-18.38, 23.5) * mm});
            skLineSegment(sketch, "E180.1", {"start": v(-18.37, 23.5) * mm, "end": v(-22.37, 23.5) * mm});
            skLineSegment(sketch, "E180.2", {"start": v(-18.37, 31.5) * mm, "end": v(-22.38, 31.5) * mm});
            skLineSegment(sketch, "E180.3", {"start": v(-22.38, 31.5) * mm, "end": v(-22.38, 23.5) * mm});
            skLineSegment(sketch, "E181.0", {"start": v(-18.38, 13.5) * mm, "end": v(-22.38, 13.5) * mm});
            skLineSegment(sketch, "E181.1", {"start": v(-18.38, 13.5) * mm, "end": v(-18.38, 5.5) * mm});
            skLineSegment(sketch, "E181.2", {"start": v(-18.38, 5.5) * mm, "end": v(-22.38, 5.5) * mm});
            skLineSegment(sketch, "E181.3", {"start": v(-22.37, 13.5) * mm, "end": v(-22.38, 5.5) * mm});
            skLineSegment(sketch, "E182.0", {"start": v(41.62, 23.5) * mm, "end": v(45.62, 23.5) * mm});
            skLineSegment(sketch, "E182.1", {"start": v(41.63, 31.5) * mm, "end": v(41.63, 23.5) * mm});
            skLineSegment(sketch, "E182.2", {"start": v(41.62, 31.5) * mm, "end": v(45.62, 31.5) * mm});
            skLineSegment(sketch, "E182.3", {"start": v(41.62, 13.5) * mm, "end": v(45.62, 13.5) * mm});
            skLineSegment(sketch, "E182.4", {"start": v(41.62, 13.5) * mm, "end": v(41.62, 5.5) * mm});
            skLineSegment(sketch, "E182.5", {"start": v(41.62, 5.5) * mm, "end": v(45.62, 5.5) * mm});
            skLineSegment(sketch, "E183.0", {"start": v(45.63, 31.5) * mm, "end": v(45.63, 23.5) * mm});
            skLineSegment(sketch, "E184.0", {"start": v(45.62, 13.5) * mm, "end": v(45.62, 5.5) * mm});
            skSolve(sketch);
        }
        {
            var Q0;
            Q0 = qSketchRegion(id + "F13", true);
            extrude(context, id + "F14", {"entities" : qUnion([Q0]), "operationType" : NewBodyOperationType.REMOVE, "oppositeDirection" : true, "depth" : 10 * mm, "offsetDistance" : 25 * mm});
        }
        {
            var Q0;
            Q0 = qSketchRegion(id + "F3", true);
            extrude(context, id + "F15", {"entities" : qUnion([Q0]), "operationType" : NewBodyOperationType.REMOVE, "endBound" : BoundingType.THROUGH_ALL, "depth" : 25 * mm, "offsetDistance" : 25 * mm});
        }
        {
            var Q0;
            Q0=qCreatedBy(makeId("Front.planeOp"),FACE);
            var sketch = newSketch(context, id + "F16", { "sketchPlane" : qUnion([Q0])});
            skLineSegment(sketch, "E185.0", {"start": v(-11.38, 32.5) * mm, "end": v(-1.38, 32.5) * mm});
            skLineSegment(sketch, "E185.1", {"start": v(-11.38, 32.5) * mm, "end": v(-11.38, 22.5) * mm});
            skLineSegment(sketch, "E185.2", {"start": v(-11.38, 22.5) * mm, "end": v(-1.38, 22.5) * mm});
            skLineSegment(sketch, "E185.3", {"start": v(-1.38, 32.5) * mm, "end": v(-1.38, 22.5) * mm});
            skSolve(sketch);
        }
        {
            var Q0;
            Q0 = qSketchRegion(id + "F16", true);
            extrude(context, id + "F17", {"entities" : qUnion([Q0]), "operationType" : NewBodyOperationType.REMOVE, "depth" : 3.5 * mm, "offsetDistance" : 25 * mm});
        }
    });
